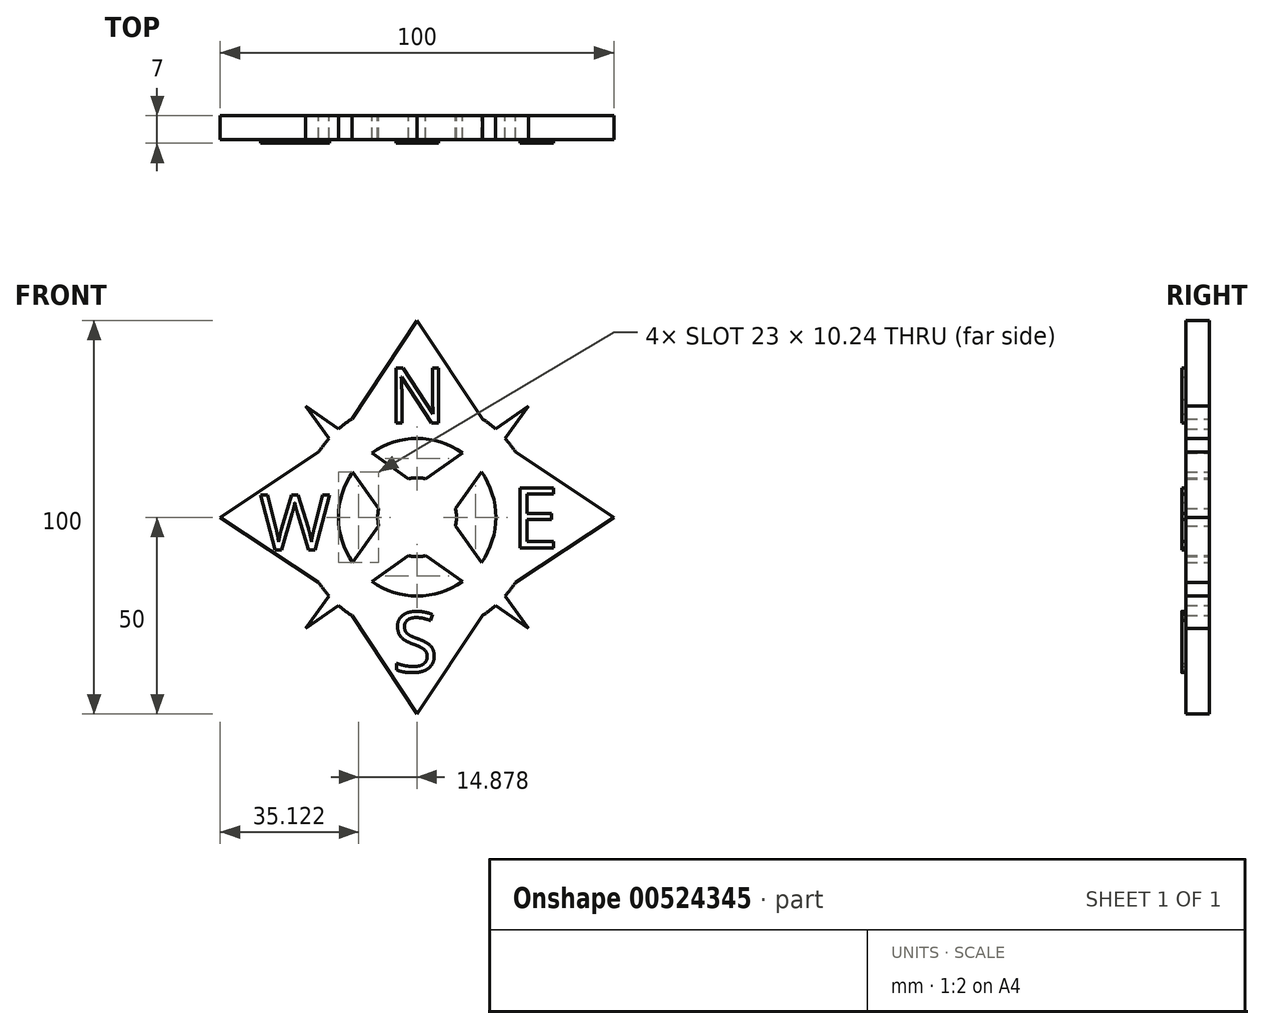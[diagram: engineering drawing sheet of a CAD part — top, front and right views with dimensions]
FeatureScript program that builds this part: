
annotation { "Feature Type Name" : "Feature", "Feature Type Description" : "" }
export const myFeature = defineFeature(function(context is Context, id is Id, definition is map)
    precondition{}
    {
        {
            var Q0;
            Q0=qCreatedBy(makeId("Front.planeOp"),FACE);
            var sketch = newSketch(context, id + "F0", { "sketchPlane" : qUnion([Q0])});
            skCircle(sketch, "E0", {"center": v(0, 0) * mm, "radius": 10 * mm});
            skCircle(sketch, "E1", {"center": v(0, 0) * mm, "radius": 20 * mm});
            skCircle(sketch, "E2", {"center": v(0, 0) * mm, "radius": 30 * mm});
            skPoint(sketch, "E3", {"position": v(0, 50) * mm});
            skPoint(sketch, "E4", {"position": v(0, -50) * mm});
            skPoint(sketch, "E5", {"position": v(-50, 0) * mm});
            skPoint(sketch, "E6", {"position": v(50, 0) * mm});
            skLineSegment(sketch, "E7", {"start": v(0, 50) * mm, "end": v(-16.58, 25) * mm});
            skLineSegment(sketch, "E8", {"start": v(0, 50) * mm, "end": v(16.58, 25) * mm});
            skLineSegment(sketch, "E9", {"start": v(50, 0) * mm, "end": v(25, 16.58) * mm});
            skLineSegment(sketch, "E10", {"start": v(50, 0) * mm, "end": v(25, -16.58) * mm});
            skLineSegment(sketch, "E11", {"start": v(0, -50) * mm, "end": v(16.58, -25) * mm});
            skLineSegment(sketch, "E12", {"start": v(0, -50) * mm, "end": v(-16.58, -25) * mm});
            skLineSegment(sketch, "E13", {"start": v(-50, 0) * mm, "end": v(-25, -16.58) * mm});
            skLineSegment(sketch, "E14", {"start": v(-50, 0) * mm, "end": v(-25, 16.58) * mm});
            skLineSegment(sketch, "E15", {"start": v(0, 0) * mm, "end": v(28.28, 28.28) * mm});
            skLineSegment(sketch, "E16", {"start": v(28.28, 28.28) * mm, "end": v(2.2, 9.76) * mm});
            skLineSegment(sketch, "E17", {"start": v(28.28, 28.28) * mm, "end": v(9.76, 2.2) * mm});
            skLineSegment(sketch, "E18", {"start": v(0, 0) * mm, "end": v(28.28, -28.28) * mm});
            skLineSegment(sketch, "E19", {"start": v(28.28, -28.28) * mm, "end": v(9.76, -2.2) * mm});
            skLineSegment(sketch, "E20", {"start": v(28.28, -28.28) * mm, "end": v(2.2, -9.76) * mm});
            skLineSegment(sketch, "E21", {"start": v(0, 0) * mm, "end": v(-28.28, -28.28) * mm});
            skLineSegment(sketch, "E22", {"start": v(-28.28, -28.28) * mm, "end": v(-2.2, -9.76) * mm});
            skLineSegment(sketch, "E23", {"start": v(-28.28, -28.28) * mm, "end": v(-9.76, -2.2) * mm});
            skLineSegment(sketch, "E24", {"start": v(0, 0) * mm, "end": v(-28.28, 28.28) * mm});
            skLineSegment(sketch, "E25", {"start": v(-28.28, 28.28) * mm, "end": v(-2.2, 9.76) * mm});
            skLineSegment(sketch, "E26", {"start": v(-28.28, 28.28) * mm, "end": v(-9.76, 2.2) * mm});
            skPoint(sketch, "E27", {"position": v(0, 30) * mm});
            skPoint(sketch, "E28", {"position": v(30, 0) * mm});
            skPoint(sketch, "E29", {"position": v(0, -30) * mm});
            skPoint(sketch, "E30", {"position": v(-30, 0) * mm});
            skSolve(sketch);
        }
        {
            var Q0;
            {var subQ0=sQuery(id+"F0.wireOp",EDGE,"E7");Q0=makeQuery(id+"F0.imprint","IMPRINT",FACE,{"disambiguationData":[TD([[makeQuery(id+"F0.imprint","IMPRINT",EDGE,{"derivedFrom":subQ0}),1.0]])]});}
            var Q1;
            {var subQ3=sQuery(id+"F0.wireOp",EDGE,"E16");var subQ7=sQuery(id+"F0.wireOp",EDGE,"E1");var subQ8=makeQuery(id+"F0.imprint","INTERSECT",VERTEX,{"derivedFrom":[subQ7,subQ3]});Q1=makeQuery(id+"F0.imprint","IMPRINT",FACE,{"disambiguationData":[TD([[makeQuery(id+"F0.imprint","IMPRINT",EDGE,{"disambiguationData":[TD([[subQ8,-1.0]])],"derivedFrom":subQ7}),-1.0]])]});}
            var Q2;
            {var subQ0=sQuery(id+"F0.wireOp",EDGE,"E25");var subQ1=sQuery(id+"F0.wireOp",EDGE,"E2");var subQ2=makeQuery(id+"F0.imprint","INTERSECT",VERTEX,{"derivedFrom":[subQ1,subQ0]});Q2=makeQuery(id+"F0.imprint","IMPRINT",FACE,{"disambiguationData":[TD([[makeQuery(id+"F0.imprint","IMPRINT",EDGE,{"disambiguationData":[TD([[subQ2,-1.0]])],"derivedFrom":subQ1}),-1.0]])]});}
            var Q3;
            {var subQ0=sQuery(id+"F0.wireOp",EDGE,"E26");var subQ1=sQuery(id+"F0.wireOp",EDGE,"E2");var subQ2=makeQuery(id+"F0.imprint","INTERSECT",VERTEX,{"derivedFrom":[subQ1,subQ0]});Q3=makeQuery(id+"F0.imprint","IMPRINT",FACE,{"disambiguationData":[TD([[makeQuery(id+"F0.imprint","IMPRINT",EDGE,{"disambiguationData":[TD([[subQ2,1.0]])],"derivedFrom":subQ1}),-1.0]])]});}
            var Q4;
            {var subQ0=sQuery(id+"F0.wireOp",EDGE,"E24");var subQ1=sQuery(id+"F0.wireOp",EDGE,"E1");var subQ2=makeQuery(id+"F0.imprint","INTERSECT",VERTEX,{"derivedFrom":[subQ1,subQ0]});Q4=makeQuery(id+"F0.imprint","IMPRINT",FACE,{"disambiguationData":[TD([[makeQuery(id+"F0.imprint","IMPRINT",EDGE,{"disambiguationData":[TD([[subQ2,-1.0]])],"derivedFrom":subQ1}),-1.0]])]});}
            var Q5;
            {var subQ0=sQuery(id+"F0.wireOp",EDGE,"E25");var subQ1=sQuery(id+"F0.wireOp",EDGE,"E1");var subQ2=makeQuery(id+"F0.imprint","INTERSECT",VERTEX,{"derivedFrom":[subQ1,subQ0]});Q5=makeQuery(id+"F0.imprint","IMPRINT",FACE,{"disambiguationData":[TD([[makeQuery(id+"F0.imprint","IMPRINT",EDGE,{"disambiguationData":[TD([[subQ2,-1.0]])],"derivedFrom":subQ1}),-1.0]])]});}
            var Q6;
            {var subQ0=sQuery(id+"F0.wireOp",EDGE,"E25");var subQ1=sQuery(id+"F0.wireOp",EDGE,"E0");var subQ2=makeQuery(id+"F0.imprint","INTERSECT",VERTEX,{"derivedFrom":[subQ1,subQ0]});Q6=makeQuery(id+"F0.imprint","IMPRINT",FACE,{"disambiguationData":[TD([[makeQuery(id+"F0.imprint","IMPRINT",EDGE,{"disambiguationData":[TD([[subQ2,-1.0]])],"derivedFrom":subQ1}),-1.0]])]});}
            var Q7;
            {var subQ0=sQuery(id+"F0.wireOp",EDGE,"E26");var subQ1=sQuery(id+"F0.wireOp",EDGE,"E0");var subQ2=makeQuery(id+"F0.imprint","INTERSECT",VERTEX,{"derivedFrom":[subQ1,subQ0]});Q7=makeQuery(id+"F0.imprint","IMPRINT",FACE,{"disambiguationData":[TD([[makeQuery(id+"F0.imprint","IMPRINT",EDGE,{"disambiguationData":[TD([[subQ2,1.0]])],"derivedFrom":subQ1}),-1.0]])]});}
            var Q8;
            {var subQ3=sQuery(id+"F0.wireOp",EDGE,"E0");var subQ6=makeQuery(id+"F0.imprint","INTERSECT",VERTEX,{"derivedFrom":[subQ3,sQuery(id+"F0.wireOp",EDGE,"E26")]});Q8=makeQuery(id+"F0.imprint","IMPRINT",FACE,{"disambiguationData":[TD([[makeQuery(id+"F0.imprint","IMPRINT",EDGE,{"disambiguationData":[TD([[subQ6,1.0]])],"derivedFrom":subQ3}),1.0]])]});}
            var Q9;
            {var subQ0=sQuery(id+"F0.wireOp",EDGE,"E0");var subQ7=makeQuery(id+"F0.imprint","INTERSECT",VERTEX,{"derivedFrom":[subQ0,sQuery(id+"F0.wireOp",EDGE,"E16")]});Q9=makeQuery(id+"F0.imprint","IMPRINT",FACE,{"disambiguationData":[TD([[makeQuery(id+"F0.imprint","IMPRINT",EDGE,{"disambiguationData":[TD([[subQ7,1.0]])],"derivedFrom":subQ0}),1.0]])]});}
            var Q10;
            {var subQ3=sQuery(id+"F0.wireOp",EDGE,"E0");var subQ5=makeQuery(id+"F0.imprint","INTERSECT",VERTEX,{"derivedFrom":[subQ3,sQuery(id+"F0.wireOp",EDGE,"E17")]});Q10=makeQuery(id+"F0.imprint","IMPRINT",FACE,{"disambiguationData":[TD([[makeQuery(id+"F0.imprint","IMPRINT",EDGE,{"disambiguationData":[TD([[subQ5,-1.0]])],"derivedFrom":subQ3}),1.0]])]});}
            var Q11;
            {var subQ0=sQuery(id+"F0.wireOp",EDGE,"E0");var subQ4=makeQuery(id+"F0.imprint","INTERSECT",VERTEX,{"derivedFrom":[subQ0,sQuery(id+"F0.wireOp",EDGE,"E22")]});Q11=makeQuery(id+"F0.imprint","IMPRINT",FACE,{"disambiguationData":[TD([[makeQuery(id+"F0.imprint","IMPRINT",EDGE,{"disambiguationData":[TD([[subQ4,1.0]])],"derivedFrom":subQ0}),1.0]])]});}
            var Q12;
            {var subQ0=sQuery(id+"F0.wireOp",EDGE,"E23");var subQ1=sQuery(id+"F0.wireOp",EDGE,"E0");var subQ2=makeQuery(id+"F0.imprint","INTERSECT",VERTEX,{"derivedFrom":[subQ1,subQ0]});Q12=makeQuery(id+"F0.imprint","IMPRINT",FACE,{"disambiguationData":[TD([[makeQuery(id+"F0.imprint","IMPRINT",EDGE,{"disambiguationData":[TD([[subQ2,-1.0]])],"derivedFrom":subQ1}),-1.0]])]});}
            var Q13;
            {var subQ0=sQuery(id+"F0.wireOp",EDGE,"E22");var subQ1=sQuery(id+"F0.wireOp",EDGE,"E0");var subQ2=makeQuery(id+"F0.imprint","INTERSECT",VERTEX,{"derivedFrom":[subQ1,subQ0]});Q13=makeQuery(id+"F0.imprint","IMPRINT",FACE,{"disambiguationData":[TD([[makeQuery(id+"F0.imprint","IMPRINT",EDGE,{"disambiguationData":[TD([[subQ2,1.0]])],"derivedFrom":subQ1}),-1.0]])]});}
            var Q14;
            {var subQ0=sQuery(id+"F0.wireOp",EDGE,"E21");var subQ1=sQuery(id+"F0.wireOp",EDGE,"E1");var subQ2=makeQuery(id+"F0.imprint","INTERSECT",VERTEX,{"derivedFrom":[subQ1,subQ0]});Q14=makeQuery(id+"F0.imprint","IMPRINT",FACE,{"disambiguationData":[TD([[makeQuery(id+"F0.imprint","IMPRINT",EDGE,{"disambiguationData":[TD([[subQ2,-1.0]])],"derivedFrom":subQ1}),-1.0]])]});}
            var Q15;
            {var subQ0=sQuery(id+"F0.wireOp",EDGE,"E23");var subQ1=sQuery(id+"F0.wireOp",EDGE,"E1");var subQ2=makeQuery(id+"F0.imprint","INTERSECT",VERTEX,{"derivedFrom":[subQ1,subQ0]});Q15=makeQuery(id+"F0.imprint","IMPRINT",FACE,{"disambiguationData":[TD([[makeQuery(id+"F0.imprint","IMPRINT",EDGE,{"disambiguationData":[TD([[subQ2,-1.0]])],"derivedFrom":subQ1}),-1.0]])]});}
            var Q16;
            {var subQ0=sQuery(id+"F0.wireOp",EDGE,"E22");var subQ1=sQuery(id+"F0.wireOp",EDGE,"E2");var subQ2=makeQuery(id+"F0.imprint","INTERSECT",VERTEX,{"derivedFrom":[subQ1,subQ0]});Q16=makeQuery(id+"F0.imprint","IMPRINT",FACE,{"disambiguationData":[TD([[makeQuery(id+"F0.imprint","IMPRINT",EDGE,{"disambiguationData":[TD([[subQ2,1.0]])],"derivedFrom":subQ1}),-1.0]])]});}
            var Q17;
            {var subQ0=sQuery(id+"F0.wireOp",EDGE,"E23");var subQ1=sQuery(id+"F0.wireOp",EDGE,"E2");var subQ2=makeQuery(id+"F0.imprint","INTERSECT",VERTEX,{"derivedFrom":[subQ1,subQ0]});Q17=makeQuery(id+"F0.imprint","IMPRINT",FACE,{"disambiguationData":[TD([[makeQuery(id+"F0.imprint","IMPRINT",EDGE,{"disambiguationData":[TD([[subQ2,-1.0]])],"derivedFrom":subQ1}),-1.0]])]});}
            var Q18;
            {var subQ0=sQuery(id+"F0.wireOp",EDGE,"E20");var subQ1=sQuery(id+"F0.wireOp",EDGE,"E0");var subQ2=makeQuery(id+"F0.imprint","INTERSECT",VERTEX,{"derivedFrom":[subQ1,subQ0]});Q18=makeQuery(id+"F0.imprint","IMPRINT",FACE,{"disambiguationData":[TD([[makeQuery(id+"F0.imprint","IMPRINT",EDGE,{"disambiguationData":[TD([[subQ2,-1.0]])],"derivedFrom":subQ1}),-1.0]])]});}
            var Q19;
            {var subQ0=sQuery(id+"F0.wireOp",EDGE,"E19");var subQ1=sQuery(id+"F0.wireOp",EDGE,"E0");var subQ2=makeQuery(id+"F0.imprint","INTERSECT",VERTEX,{"derivedFrom":[subQ1,subQ0]});Q19=makeQuery(id+"F0.imprint","IMPRINT",FACE,{"disambiguationData":[TD([[makeQuery(id+"F0.imprint","IMPRINT",EDGE,{"disambiguationData":[TD([[subQ2,1.0]])],"derivedFrom":subQ1}),-1.0]])]});}
            var Q20;
            {var subQ0=sQuery(id+"F0.wireOp",EDGE,"E18");var subQ1=sQuery(id+"F0.wireOp",EDGE,"E1");var subQ2=makeQuery(id+"F0.imprint","INTERSECT",VERTEX,{"derivedFrom":[subQ1,subQ0]});Q20=makeQuery(id+"F0.imprint","IMPRINT",FACE,{"disambiguationData":[TD([[makeQuery(id+"F0.imprint","IMPRINT",EDGE,{"disambiguationData":[TD([[subQ2,-1.0]])],"derivedFrom":subQ1}),-1.0]])]});}
            var Q21;
            {var subQ0=sQuery(id+"F0.wireOp",EDGE,"E20");var subQ1=sQuery(id+"F0.wireOp",EDGE,"E1");var subQ2=makeQuery(id+"F0.imprint","INTERSECT",VERTEX,{"derivedFrom":[subQ1,subQ0]});Q21=makeQuery(id+"F0.imprint","IMPRINT",FACE,{"disambiguationData":[TD([[makeQuery(id+"F0.imprint","IMPRINT",EDGE,{"disambiguationData":[TD([[subQ2,-1.0]])],"derivedFrom":subQ1}),-1.0]])]});}
            var Q22;
            {var subQ0=sQuery(id+"F0.wireOp",EDGE,"E20");var subQ1=sQuery(id+"F0.wireOp",EDGE,"E2");var subQ2=makeQuery(id+"F0.imprint","INTERSECT",VERTEX,{"derivedFrom":[subQ1,subQ0]});Q22=makeQuery(id+"F0.imprint","IMPRINT",FACE,{"disambiguationData":[TD([[makeQuery(id+"F0.imprint","IMPRINT",EDGE,{"disambiguationData":[TD([[subQ2,-1.0]])],"derivedFrom":subQ1}),-1.0]])]});}
            var Q23;
            {var subQ0=sQuery(id+"F0.wireOp",EDGE,"E19");var subQ1=sQuery(id+"F0.wireOp",EDGE,"E2");var subQ2=makeQuery(id+"F0.imprint","INTERSECT",VERTEX,{"derivedFrom":[subQ1,subQ0]});Q23=makeQuery(id+"F0.imprint","IMPRINT",FACE,{"disambiguationData":[TD([[makeQuery(id+"F0.imprint","IMPRINT",EDGE,{"disambiguationData":[TD([[subQ2,1.0]])],"derivedFrom":subQ1}),-1.0]])]});}
            var Q24;
            {var subQ0=sQuery(id+"F0.wireOp",EDGE,"E16");var subQ1=sQuery(id+"F0.wireOp",EDGE,"E2");var subQ2=makeQuery(id+"F0.imprint","INTERSECT",VERTEX,{"derivedFrom":[subQ1,subQ0]});Q24=makeQuery(id+"F0.imprint","IMPRINT",FACE,{"disambiguationData":[TD([[makeQuery(id+"F0.imprint","IMPRINT",EDGE,{"disambiguationData":[TD([[subQ2,1.0]])],"derivedFrom":subQ1}),-1.0]])]});}
            var Q25;
            {var subQ0=sQuery(id+"F0.wireOp",EDGE,"E17");var subQ1=sQuery(id+"F0.wireOp",EDGE,"E2");var subQ2=makeQuery(id+"F0.imprint","INTERSECT",VERTEX,{"derivedFrom":[subQ1,subQ0]});Q25=makeQuery(id+"F0.imprint","IMPRINT",FACE,{"disambiguationData":[TD([[makeQuery(id+"F0.imprint","IMPRINT",EDGE,{"disambiguationData":[TD([[subQ2,-1.0]])],"derivedFrom":subQ1}),-1.0]])]});}
            var Q26;
            {var subQ0=sQuery(id+"F0.wireOp",EDGE,"E15");var subQ1=sQuery(id+"F0.wireOp",EDGE,"E1");var subQ2=makeQuery(id+"F0.imprint","INTERSECT",VERTEX,{"derivedFrom":[subQ1,subQ0]});Q26=makeQuery(id+"F0.imprint","IMPRINT",FACE,{"disambiguationData":[TD([[makeQuery(id+"F0.imprint","IMPRINT",EDGE,{"disambiguationData":[TD([[subQ2,-1.0]])],"derivedFrom":subQ1}),-1.0]])]});}
            var Q27;
            {var subQ0=sQuery(id+"F0.wireOp",EDGE,"E15");var subQ1=sQuery(id+"F0.wireOp",EDGE,"E1");var subQ2=makeQuery(id+"F0.imprint","INTERSECT",VERTEX,{"derivedFrom":[subQ1,subQ0]});Q27=makeQuery(id+"F0.imprint","IMPRINT",FACE,{"disambiguationData":[TD([[makeQuery(id+"F0.imprint","IMPRINT",EDGE,{"disambiguationData":[TD([[subQ2,1.0]])],"derivedFrom":subQ1}),-1.0]])]});}
            var Q28;
            {var subQ0=sQuery(id+"F0.wireOp",EDGE,"E16");var subQ1=sQuery(id+"F0.wireOp",EDGE,"E0");var subQ2=makeQuery(id+"F0.imprint","INTERSECT",VERTEX,{"derivedFrom":[subQ1,subQ0]});Q28=makeQuery(id+"F0.imprint","IMPRINT",FACE,{"disambiguationData":[TD([[makeQuery(id+"F0.imprint","IMPRINT",EDGE,{"disambiguationData":[TD([[subQ2,1.0]])],"derivedFrom":subQ1}),-1.0]])]});}
            var Q29;
            {var subQ0=sQuery(id+"F0.wireOp",EDGE,"E17");var subQ1=sQuery(id+"F0.wireOp",EDGE,"E0");var subQ2=makeQuery(id+"F0.imprint","INTERSECT",VERTEX,{"derivedFrom":[subQ1,subQ0]});Q29=makeQuery(id+"F0.imprint","IMPRINT",FACE,{"disambiguationData":[TD([[makeQuery(id+"F0.imprint","IMPRINT",EDGE,{"disambiguationData":[TD([[subQ2,-1.0]])],"derivedFrom":subQ1}),-1.0]])]});}
            var Q30;
            {var subQ5=sQuery(id+"F0.wireOp",EDGE,"E17");var subQ7=sQuery(id+"F0.wireOp",EDGE,"E1");var subQ8=makeQuery(id+"F0.imprint","INTERSECT",VERTEX,{"derivedFrom":[subQ7,subQ5]});Q30=makeQuery(id+"F0.imprint","IMPRINT",FACE,{"disambiguationData":[TD([[makeQuery(id+"F0.imprint","IMPRINT",EDGE,{"disambiguationData":[TD([[subQ8,1.0]])],"derivedFrom":subQ7}),-1.0]])]});}
            var Q31;
            {var subQ0=sQuery(id+"F0.wireOp",EDGE,"E9");Q31=makeQuery(id+"F0.imprint","IMPRINT",FACE,{"disambiguationData":[TD([[makeQuery(id+"F0.imprint","IMPRINT",EDGE,{"derivedFrom":subQ0}),1.0]])]});}
            var Q32;
            {var subQ5=sQuery(id+"F0.wireOp",EDGE,"E22");var subQ7=sQuery(id+"F0.wireOp",EDGE,"E1");var subQ9=makeQuery(id+"F0.imprint","INTERSECT",VERTEX,{"derivedFrom":[subQ7,subQ5]});Q32=makeQuery(id+"F0.imprint","IMPRINT",FACE,{"disambiguationData":[TD([[makeQuery(id+"F0.imprint","IMPRINT",EDGE,{"disambiguationData":[TD([[subQ9,-1.0]])],"derivedFrom":subQ7}),-1.0]])]});}
            var Q33;
            {var subQ0=sQuery(id+"F0.wireOp",EDGE,"E11");Q33=makeQuery(id+"F0.imprint","IMPRINT",FACE,{"disambiguationData":[TD([[makeQuery(id+"F0.imprint","IMPRINT",EDGE,{"derivedFrom":subQ0}),1.0]])]});}
            var Q34;
            {var subQ5=sQuery(id+"F0.wireOp",EDGE,"E26");var subQ7=sQuery(id+"F0.wireOp",EDGE,"E1");var subQ8=makeQuery(id+"F0.imprint","INTERSECT",VERTEX,{"derivedFrom":[subQ7,subQ5]});Q34=makeQuery(id+"F0.imprint","IMPRINT",FACE,{"disambiguationData":[TD([[makeQuery(id+"F0.imprint","IMPRINT",EDGE,{"disambiguationData":[TD([[subQ8,-1.0]])],"derivedFrom":subQ7}),-1.0]])]});}
            var Q35;
            {var subQ0=sQuery(id+"F0.wireOp",EDGE,"E13");Q35=makeQuery(id+"F0.imprint","IMPRINT",FACE,{"disambiguationData":[TD([[makeQuery(id+"F0.imprint","IMPRINT",EDGE,{"derivedFrom":subQ0}),1.0]])]});}
            extrude(context, id + "F1", {"entities" : qUnion([Q0, Q1, Q2, Q3, Q4, Q5, Q6, Q7, Q8, Q9, Q10, Q11, Q12, Q13, Q14, Q15, Q16, Q17, Q18, Q19, Q20, Q21, Q22, Q23, Q24, Q25, Q26, Q27, Q28, Q29, Q30, Q31, Q32, Q33, Q34, Q35]), "depth" : 6 * mm, "offsetDistance" : 25 * mm});
        }
        {
            var Q0;
            Q0=makeQuery(id+"F1.opExtrude","CAP_FACE",FACE,{"disambiguationData":[OSD([sQuery(id+"F0.wireOp",EDGE,"E0"),sQuery(id+"F0.wireOp",EDGE,"E1"),sQuery(id+"F0.wireOp",EDGE,"E2"),sQuery(id+"F0.wireOp",EDGE,"E7"),sQuery(id+"F0.wireOp",EDGE,"E8"),sQuery(id+"F0.wireOp",EDGE,"E9"),sQuery(id+"F0.wireOp",EDGE,"E10"),sQuery(id+"F0.wireOp",EDGE,"E11"),sQuery(id+"F0.wireOp",EDGE,"E12"),sQuery(id+"F0.wireOp",EDGE,"E13"),sQuery(id+"F0.wireOp",EDGE,"E14"),sQuery(id+"F0.wireOp",EDGE,"E16"),sQuery(id+"F0.wireOp",EDGE,"E17"),sQuery(id+"F0.wireOp",EDGE,"E19"),sQuery(id+"F0.wireOp",EDGE,"E20"),sQuery(id+"F0.wireOp",EDGE,"E22"),sQuery(id+"F0.wireOp",EDGE,"E23"),sQuery(id+"F0.wireOp",EDGE,"E25"),sQuery(id+"F0.wireOp",EDGE,"E26")])],"isStart":false});
            var sketch = newSketch(context, id + "F2", { "sketchPlane" : qUnion([Q0])});
            skText(sketch, "E31", { "text": "N", "fontName": "OpenSans-Regular.ttf"});
            const initialGuessF2  = {"E31": [-0.00728, 0.024, 1, 0, 0.01399]};
            skSetInitialGuess(sketch, initialGuessF2);
            skSolve(sketch);
        }
        {
            var Q0;
            Q0 = qSketchRegion(id + "F2", true);
            extrude(context, id + "F3", {"entities" : qUnion([Q0]), "operationType" : NewBodyOperationType.ADD, "depth" : 1 * mm, "offsetDistance" : 25 * mm});
        }
        {
            var Q0;
            Q0=makeQuery(id+"F1.opExtrude","CAP_FACE",FACE,{"disambiguationData":[OSD([sQuery(id+"F0.wireOp",EDGE,"E0"),sQuery(id+"F0.wireOp",EDGE,"E1"),sQuery(id+"F0.wireOp",EDGE,"E2"),sQuery(id+"F0.wireOp",EDGE,"E7"),sQuery(id+"F0.wireOp",EDGE,"E8"),sQuery(id+"F0.wireOp",EDGE,"E9"),sQuery(id+"F0.wireOp",EDGE,"E10"),sQuery(id+"F0.wireOp",EDGE,"E11"),sQuery(id+"F0.wireOp",EDGE,"E12"),sQuery(id+"F0.wireOp",EDGE,"E13"),sQuery(id+"F0.wireOp",EDGE,"E14"),sQuery(id+"F0.wireOp",EDGE,"E16"),sQuery(id+"F0.wireOp",EDGE,"E17"),sQuery(id+"F0.wireOp",EDGE,"E19"),sQuery(id+"F0.wireOp",EDGE,"E20"),sQuery(id+"F0.wireOp",EDGE,"E22"),sQuery(id+"F0.wireOp",EDGE,"E23"),sQuery(id+"F0.wireOp",EDGE,"E25"),sQuery(id+"F0.wireOp",EDGE,"E26")])],"isStart":false});
            var sketch = newSketch(context, id + "F4", { "sketchPlane" : qUnion([Q0])});
            skText(sketch, "E32", { "text": "S", "fontName": "OpenSans-Regular.ttf"});
            const initialGuessF4  = {"E32": [-0.00628, -0.03927, 1, 0, 0.01527]};
            skSetInitialGuess(sketch, initialGuessF4);
            skSolve(sketch);
        }
        {
            var Q0;
            Q0 = qSketchRegion(id + "F4", true);
            extrude(context, id + "F5", {"entities" : qUnion([Q0]), "operationType" : NewBodyOperationType.ADD, "depth" : 1 * mm, "offsetDistance" : 25 * mm});
        }
        {
            var Q0;
            Q0=makeQuery(id+"F1.opExtrude","CAP_FACE",FACE,{"disambiguationData":[OSD([sQuery(id+"F0.wireOp",EDGE,"E0"),sQuery(id+"F0.wireOp",EDGE,"E1"),sQuery(id+"F0.wireOp",EDGE,"E2"),sQuery(id+"F0.wireOp",EDGE,"E7"),sQuery(id+"F0.wireOp",EDGE,"E8"),sQuery(id+"F0.wireOp",EDGE,"E9"),sQuery(id+"F0.wireOp",EDGE,"E10"),sQuery(id+"F0.wireOp",EDGE,"E11"),sQuery(id+"F0.wireOp",EDGE,"E12"),sQuery(id+"F0.wireOp",EDGE,"E13"),sQuery(id+"F0.wireOp",EDGE,"E14"),sQuery(id+"F0.wireOp",EDGE,"E16"),sQuery(id+"F0.wireOp",EDGE,"E17"),sQuery(id+"F0.wireOp",EDGE,"E19"),sQuery(id+"F0.wireOp",EDGE,"E20"),sQuery(id+"F0.wireOp",EDGE,"E22"),sQuery(id+"F0.wireOp",EDGE,"E23"),sQuery(id+"F0.wireOp",EDGE,"E25"),sQuery(id+"F0.wireOp",EDGE,"E26")])],"isStart":false});
            var sketch = newSketch(context, id + "F6", { "sketchPlane" : qUnion([Q0])});
            skText(sketch, "E33", { "text": "E", "fontName": "OpenSans-Regular.ttf"});
            const initialGuessF6  = {"E33": [0.024, -0.00778, 1, 0, 0.0154]};
            skSetInitialGuess(sketch, initialGuessF6);
            skSolve(sketch);
        }
        {
            var Q0;
            Q0 = qSketchRegion(id + "F6", true);
            extrude(context, id + "F7", {"entities" : qUnion([Q0]), "operationType" : NewBodyOperationType.ADD, "depth" : 1 * mm, "offsetDistance" : 25 * mm});
        }
        {
            var Q0;
            Q0=makeQuery(id+"F1.opExtrude","CAP_FACE",FACE,{"disambiguationData":[OSD([sQuery(id+"F0.wireOp",EDGE,"E0"),sQuery(id+"F0.wireOp",EDGE,"E1"),sQuery(id+"F0.wireOp",EDGE,"E2"),sQuery(id+"F0.wireOp",EDGE,"E7"),sQuery(id+"F0.wireOp",EDGE,"E8"),sQuery(id+"F0.wireOp",EDGE,"E9"),sQuery(id+"F0.wireOp",EDGE,"E10"),sQuery(id+"F0.wireOp",EDGE,"E11"),sQuery(id+"F0.wireOp",EDGE,"E12"),sQuery(id+"F0.wireOp",EDGE,"E13"),sQuery(id+"F0.wireOp",EDGE,"E14"),sQuery(id+"F0.wireOp",EDGE,"E16"),sQuery(id+"F0.wireOp",EDGE,"E17"),sQuery(id+"F0.wireOp",EDGE,"E19"),sQuery(id+"F0.wireOp",EDGE,"E20"),sQuery(id+"F0.wireOp",EDGE,"E22"),sQuery(id+"F0.wireOp",EDGE,"E23"),sQuery(id+"F0.wireOp",EDGE,"E25"),sQuery(id+"F0.wireOp",EDGE,"E26")])],"isStart":false});
            var sketch = newSketch(context, id + "F8", { "sketchPlane" : qUnion([Q0])});
            skText(sketch, "E34", { "text": "W", "fontName": "OpenSans-Regular.ttf"});
            const initialGuessF8  = {"E34": [-0.04, -0.00828, 1, 0, 0.014]};
            skSetInitialGuess(sketch, initialGuessF8);
            skSolve(sketch);
        }
        {
            var Q0;
            Q0 = qSketchRegion(id + "F8", true);
            extrude(context, id + "F9", {"entities" : qUnion([Q0]), "operationType" : NewBodyOperationType.ADD, "depth" : 1 * mm, "offsetDistance" : 25 * mm});
        }
    });
